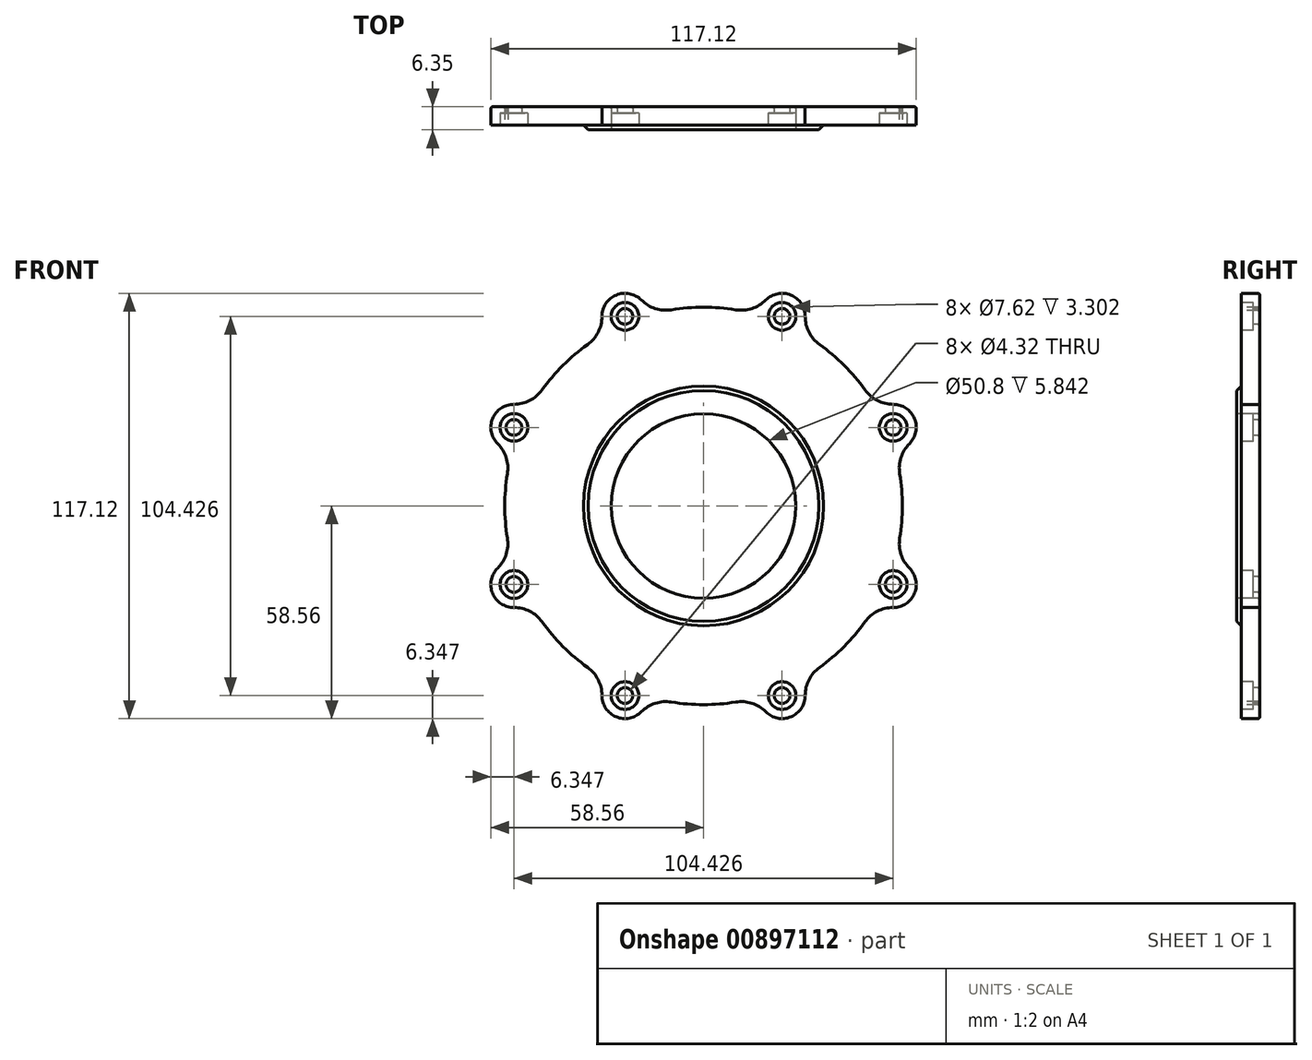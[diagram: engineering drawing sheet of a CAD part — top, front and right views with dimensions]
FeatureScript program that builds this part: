
annotation { "Feature Type Name" : "Feature", "Feature Type Description" : "" }
export const myFeature = defineFeature(function(context is Context, id is Id, definition is map)
    precondition{}
    {
        {
            var Q0;
            Q0=qCreatedBy(makeId("Front.planeOp"),FACE);
            var sketch = newSketch(context, id + "F0", { "sketchPlane" : qUnion([Q0])});
            skCircle(sketch, "E0", {"center": v(0, 0) * mm, "radius": 50.17 * mm, "construction": true});
            skArc(sketch, "E1", {"start": v(54.02, -8.84) * mm, "mid": v(54.74, 0) * mm, "end": v(54.02, 8.84) * mm});
            skCircle(sketch, "E2.cCircle", {"center": v(0, 0) * mm, "radius": 56.52 * mm, "construction": true});
            skLineSegment(sketch, "E2.0", {"start": v(52.21, -21.63) * mm, "end": v(21.63, -52.21) * mm, "construction": true});
            skLineSegment(sketch, "E2.1", {"start": v(21.63, -52.21) * mm, "end": v(-21.63, -52.21) * mm, "construction": true});
            skLineSegment(sketch, "E2.2", {"start": v(-21.63, -52.21) * mm, "end": v(-52.21, -21.63) * mm, "construction": true});
            skLineSegment(sketch, "E2.3", {"start": v(-52.21, -21.63) * mm, "end": v(-52.21, 21.63) * mm, "construction": true});
            skLineSegment(sketch, "E2.4", {"start": v(-52.21, 21.63) * mm, "end": v(-21.63, 52.21) * mm, "construction": true});
            skLineSegment(sketch, "E2.5", {"start": v(-21.63, 52.21) * mm, "end": v(21.63, 52.21) * mm, "construction": true});
            skLineSegment(sketch, "E2.6", {"start": v(21.63, 52.21) * mm, "end": v(52.21, 21.63) * mm, "construction": true});
            skLineSegment(sketch, "E2.7", {"start": v(52.21, 21.63) * mm, "end": v(52.21, -21.63) * mm, "construction": true});
            skArc(sketch, "E3", {"start": v(27.98, 52.2) * mm, "mid": v(24.06, 58.08) * mm, "end": v(17.13, 56.7) * mm});
            skArc(sketch, "E4", {"start": v(56.7, 17.13) * mm, "mid": v(58.08, 24.06) * mm, "end": v(52.2, 27.98) * mm});
            skArc(sketch, "E5", {"start": v(52.2, -27.98) * mm, "mid": v(58.08, -24.06) * mm, "end": v(56.7, -17.13) * mm});
            skArc(sketch, "E6", {"start": v(-56.7, -17.13) * mm, "mid": v(-58.08, -24.06) * mm, "end": v(-52.2, -27.98) * mm});
            skArc(sketch, "E7", {"start": v(-52.2, 27.98) * mm, "mid": v(-58.08, 24.06) * mm, "end": v(-56.7, 17.13) * mm});
            skArc(sketch, "E8.trimOffspring", {"start": v(44.45, 31.94) * mm, "mid": v(38.7, 38.7) * mm, "end": v(31.94, 44.45) * mm});
            skArc(sketch, "E9.trimOffspring", {"start": v(8.84, 54.02) * mm, "mid": v(0, 54.74) * mm, "end": v(-8.84, 54.02) * mm});
            skArc(sketch, "E10.trimOffspring", {"start": v(-54.02, 8.84) * mm, "mid": v(-54.74, 0) * mm, "end": v(-54.02, -8.84) * mm});
            skArc(sketch, "E11.trimOffspring", {"start": v(-44.45, -31.94) * mm, "mid": v(-38.7, -38.7) * mm, "end": v(-31.94, -44.45) * mm});
            skArc(sketch, "E12.trimOffspring", {"start": v(0, -54.74) * mm, "mid": v(4.44, -54.56) * mm, "end": v(8.84, -54.02) * mm});
            skPoint(sketch, "E13.visualSharp", {"position": v(-47.97, -26.36) * mm});
            skArc(sketch, "E13.filletArc", {"start": v(-44.45, -31.94) * mm, "mid": v(-47.85, -29.02) * mm, "end": v(-52.2, -27.98) * mm});
            skPoint(sketch, "E14.visualSharp", {"position": v(-52.56, -15.29) * mm});
            skArc(sketch, "E14.filletArc", {"start": v(-56.7, -17.13) * mm, "mid": v(-54.35, -13.3) * mm, "end": v(-54.02, -8.84) * mm});
            skPoint(sketch, "E15.visualSharp", {"position": v(-52.56, 15.29) * mm});
            skArc(sketch, "E15.filletArc", {"start": v(-54.02, 8.84) * mm, "mid": v(-54.35, 13.3) * mm, "end": v(-56.7, 17.13) * mm});
            skPoint(sketch, "E16.visualSharp", {"position": v(47.97, -26.36) * mm});
            skArc(sketch, "E16.filletArc", {"start": v(52.2, -27.98) * mm, "mid": v(47.85, -29.02) * mm, "end": v(44.45, -31.94) * mm});
            skPoint(sketch, "E17.visualSharp", {"position": v(52.56, -15.29) * mm});
            skArc(sketch, "E17.filletArc", {"start": v(54.02, -8.84) * mm, "mid": v(54.35, -13.3) * mm, "end": v(56.7, -17.13) * mm});
            skPoint(sketch, "E18.visualSharp", {"position": v(52.56, 15.29) * mm});
            skArc(sketch, "E18.filletArc", {"start": v(56.7, 17.13) * mm, "mid": v(54.35, 13.3) * mm, "end": v(54.02, 8.84) * mm});
            skPoint(sketch, "E19.visualSharp", {"position": v(47.97, 26.36) * mm});
            skArc(sketch, "E19.filletArc", {"start": v(44.45, 31.94) * mm, "mid": v(47.85, 29.02) * mm, "end": v(52.2, 27.98) * mm});
            skPoint(sketch, "E20.visualSharp", {"position": v(26.36, 47.97) * mm});
            skArc(sketch, "E20.filletArc", {"start": v(27.98, 52.2) * mm, "mid": v(29.02, 47.85) * mm, "end": v(31.94, 44.45) * mm});
            skPoint(sketch, "E21.visualSharp", {"position": v(15.29, 52.56) * mm});
            skArc(sketch, "E21.filletArc", {"start": v(8.84, 54.02) * mm, "mid": v(13.3, 54.35) * mm, "end": v(17.13, 56.7) * mm});
            skPoint(sketch, "E22.visualSharp", {"position": v(-15.29, 52.56) * mm});
            skArc(sketch, "E23", {"start": v(-17.13, 56.7) * mm, "mid": v(-24.06, 58.08) * mm, "end": v(-27.98, 52.2) * mm});
            skArc(sketch, "E24.filletArc", {"start": v(-17.13, 56.7) * mm, "mid": v(-13.3, 54.35) * mm, "end": v(-8.84, 54.02) * mm});
            skArc(sketch, "E25", {"start": v(-31.94, 44.45) * mm, "mid": v(-38.7, 38.7) * mm, "end": v(-44.45, 31.94) * mm});
            skArc(sketch, "E26", {"start": v(-27.98, -52.2) * mm, "mid": v(-24.06, -58.08) * mm, "end": v(-17.13, -56.7) * mm});
            skArc(sketch, "E27", {"start": v(17.13, -56.7) * mm, "mid": v(24.06, -58.08) * mm, "end": v(27.98, -52.2) * mm});
            skArc(sketch, "E28.trimOffspring", {"start": v(-8.84, -54.02) * mm, "mid": v(-4.44, -54.56) * mm, "end": v(0, -54.74) * mm});
            skArc(sketch, "E29.trimOffspring", {"start": v(31.94, -44.45) * mm, "mid": v(38.7, -38.7) * mm, "end": v(44.45, -31.94) * mm});
            skPoint(sketch, "E30.visualSharp", {"position": v(26.36, -47.97) * mm});
            skArc(sketch, "E30.filletArc", {"start": v(31.94, -44.45) * mm, "mid": v(29.02, -47.85) * mm, "end": v(27.98, -52.2) * mm});
            skPoint(sketch, "E31.visualSharp", {"position": v(15.29, -52.56) * mm});
            skArc(sketch, "E31.filletArc", {"start": v(17.13, -56.7) * mm, "mid": v(13.3, -54.35) * mm, "end": v(8.84, -54.02) * mm});
            skPoint(sketch, "E32.visualSharp", {"position": v(-15.29, -52.56) * mm});
            skArc(sketch, "E32.filletArc", {"start": v(-8.84, -54.02) * mm, "mid": v(-13.3, -54.35) * mm, "end": v(-17.13, -56.7) * mm});
            skPoint(sketch, "E33.visualSharp", {"position": v(-26.36, -47.97) * mm});
            skArc(sketch, "E33.filletArc", {"start": v(-27.98, -52.2) * mm, "mid": v(-29.02, -47.85) * mm, "end": v(-31.94, -44.45) * mm});
            skPoint(sketch, "E34.visualSharp", {"position": v(-47.97, 26.36) * mm});
            skArc(sketch, "E34.filletArc", {"start": v(-52.2, 27.98) * mm, "mid": v(-47.85, 29.02) * mm, "end": v(-44.45, 31.94) * mm});
            skPoint(sketch, "E35.visualSharp", {"position": v(-26.36, 47.97) * mm});
            skArc(sketch, "E35.filletArc", {"start": v(-31.94, 44.45) * mm, "mid": v(-29.02, 47.85) * mm, "end": v(-27.98, 52.2) * mm});
            skCircle(sketch, "E36", {"center": v(-21.63, 52.21) * mm, "radius": 2.16 * mm});
            skCircle(sketch, "E37.1.0", {"center": v(-52.21, 21.63) * mm, "radius": 2.16 * mm});
            skCircle(sketch, "E37.2.0", {"center": v(-52.21, -21.63) * mm, "radius": 2.16 * mm});
            skCircle(sketch, "E37.3.0", {"center": v(-21.63, -52.21) * mm, "radius": 2.16 * mm});
            skCircle(sketch, "E37.4.0", {"center": v(21.63, -52.21) * mm, "radius": 2.16 * mm});
            skCircle(sketch, "E37.5.0", {"center": v(52.21, -21.63) * mm, "radius": 2.16 * mm});
            skCircle(sketch, "E37.6.0", {"center": v(52.21, 21.63) * mm, "radius": 2.16 * mm});
            skCircle(sketch, "E37.7.0", {"center": v(21.63, 52.21) * mm, "radius": 2.16 * mm});
            skCircle(sketch, "E38", {"center": v(0, 0) * mm, "radius": 25.4 * mm});
            skSolve(sketch);
        }
        {
            var Q0;
            Q0=qSketchRegion(id+"F0",true);
            extrude(context, id + "F1", {"entities" : qUnion([Q0]), "oppositeDirection" : true, "depth" : 6.35 * mm});
        }
        {
            var Q0;
            Q0=qCreatedBy(makeId("Front.planeOp"),FACE);
            var sketch = newSketch(context, id + "F2", { "sketchPlane" : qUnion([Q0])});
            skCircle(sketch, "E39", {"center": v(-21.63, 52.21) * mm, "radius": 3.81 * mm});
            skCircle(sketch, "E40.1.0", {"center": v(-52.21, 21.63) * mm, "radius": 3.81 * mm});
            skCircle(sketch, "E40.2.0", {"center": v(-52.21, -21.63) * mm, "radius": 3.81 * mm});
            skCircle(sketch, "E40.3.0", {"center": v(-21.63, -52.21) * mm, "radius": 3.81 * mm});
            skCircle(sketch, "E40.4.0", {"center": v(21.63, -52.21) * mm, "radius": 3.81 * mm});
            skCircle(sketch, "E40.5.0", {"center": v(52.21, -21.63) * mm, "radius": 3.81 * mm});
            skCircle(sketch, "E40.6.0", {"center": v(52.21, 21.63) * mm, "radius": 3.81 * mm});
            skCircle(sketch, "E40.7.0", {"center": v(21.63, 52.21) * mm, "radius": 3.81 * mm});
            skPoint(sketch, "E40.center", {"position": v(0, 0) * mm});
            skSolve(sketch);
        }
        {
            var Q0;
            Q0=qSketchRegion(id+"F2",true);
            extrude(context, id + "F3", {"entities" : qUnion([Q0]), "operationType" : NewBodyOperationType.REMOVE, "oppositeDirection" : true, "depth" : 4.57 * mm});
        }
        {
            var Q0;
            Q0=qCreatedBy(makeId("Right.planeOp"),FACE);
            var sketch = newSketch(context, id + "F4", { "sketchPlane" : qUnion([Q0])});
            skLineSegment(sketch, "E41", {"start": v(0, 31.75) * mm, "end": v(1.27, 33.02) * mm});
            skLineSegment(sketch, "E42", {"start": v(1.27, 33.02) * mm, "end": v(1.27, 63.5) * mm});
            skLineSegment(sketch, "E43", {"start": v(0, 0) * mm, "end": v(-25.4, 0) * mm, "construction": true});
            skLineSegment(sketch, "E44", {"start": v(0, 31.75) * mm, "end": v(0, 63.5) * mm});
            skLineSegment(sketch, "E45", {"start": v(0, 63.5) * mm, "end": v(1.27, 63.5) * mm});
            skSolve(sketch);
        }
        {
            var Q0;
            Q0=qSketchRegion(id+"F4",true);
            var Q1;
            Q1=sQuery(id+"F4.wireOp",EDGE,"E43");
            revolve(context, id + "F5", {"operationType" : NewBodyOperationType.REMOVE, "entities" : qUnion([Q0]), "axis" : qUnion([Q1]), "revolveType" : RevolveType.FULL, "oppositeDirection" : true});
        }
        {
            var Q0;
            Q0=makeQuery(id+"F1.opExtrude","CAP_FACE",FACE,{"disambiguationData":[OSD([sQuery(id+"F0.wireOp",EDGE,"E1"),sQuery(id+"F0.wireOp",EDGE,"E3"),sQuery(id+"F0.wireOp",EDGE,"E4"),sQuery(id+"F0.wireOp",EDGE,"E5"),sQuery(id+"F0.wireOp",EDGE,"E6"),sQuery(id+"F0.wireOp",EDGE,"E7"),sQuery(id+"F0.wireOp",EDGE,"E8.trimOffspring"),sQuery(id+"F0.wireOp",EDGE,"E9.trimOffspring"),sQuery(id+"F0.wireOp",EDGE,"E10.trimOffspring"),sQuery(id+"F0.wireOp",EDGE,"E11.trimOffspring"),sQuery(id+"F0.wireOp",EDGE,"E12.trimOffspring"),sQuery(id+"F0.wireOp",EDGE,"E13.filletArc"),sQuery(id+"F0.wireOp",EDGE,"E14.filletArc"),sQuery(id+"F0.wireOp",EDGE,"E15.filletArc"),sQuery(id+"F0.wireOp",EDGE,"E16.filletArc"),sQuery(id+"F0.wireOp",EDGE,"E17.filletArc"),sQuery(id+"F0.wireOp",EDGE,"E18.filletArc"),sQuery(id+"F0.wireOp",EDGE,"E19.filletArc"),sQuery(id+"F0.wireOp",EDGE,"E20.filletArc"),sQuery(id+"F0.wireOp",EDGE,"E21.filletArc"),sQuery(id+"F0.wireOp",EDGE,"E23"),sQuery(id+"F0.wireOp",EDGE,"E24.filletArc"),sQuery(id+"F0.wireOp",EDGE,"E25"),sQuery(id+"F0.wireOp",EDGE,"E26"),sQuery(id+"F0.wireOp",EDGE,"E27"),sQuery(id+"F0.wireOp",EDGE,"E28.trimOffspring"),sQuery(id+"F0.wireOp",EDGE,"E29.trimOffspring"),sQuery(id+"F0.wireOp",EDGE,"E30.filletArc"),sQuery(id+"F0.wireOp",EDGE,"E31.filletArc"),sQuery(id+"F0.wireOp",EDGE,"E32.filletArc"),sQuery(id+"F0.wireOp",EDGE,"E33.filletArc"),sQuery(id+"F0.wireOp",EDGE,"E34.filletArc"),sQuery(id+"F0.wireOp",EDGE,"E35.filletArc"),sQuery(id+"F0.wireOp",EDGE,"E36"),sQuery(id+"F0.wireOp",EDGE,"E37.1.0"),sQuery(id+"F0.wireOp",EDGE,"E37.2.0"),sQuery(id+"F0.wireOp",EDGE,"E37.3.0"),sQuery(id+"F0.wireOp",EDGE,"E37.4.0"),sQuery(id+"F0.wireOp",EDGE,"E37.5.0"),sQuery(id+"F0.wireOp",EDGE,"E37.6.0"),sQuery(id+"F0.wireOp",EDGE,"E37.7.0"),sQuery(id+"F0.wireOp",EDGE,"E38")])],"isStart":false});
            fillet(context, id + "F6", {"entities" : qUnion([Q0]), "radius" : 0.5 * mm, "tangentPropagation" : true, "allowEdgeOverflow" : false});
        }
    });
